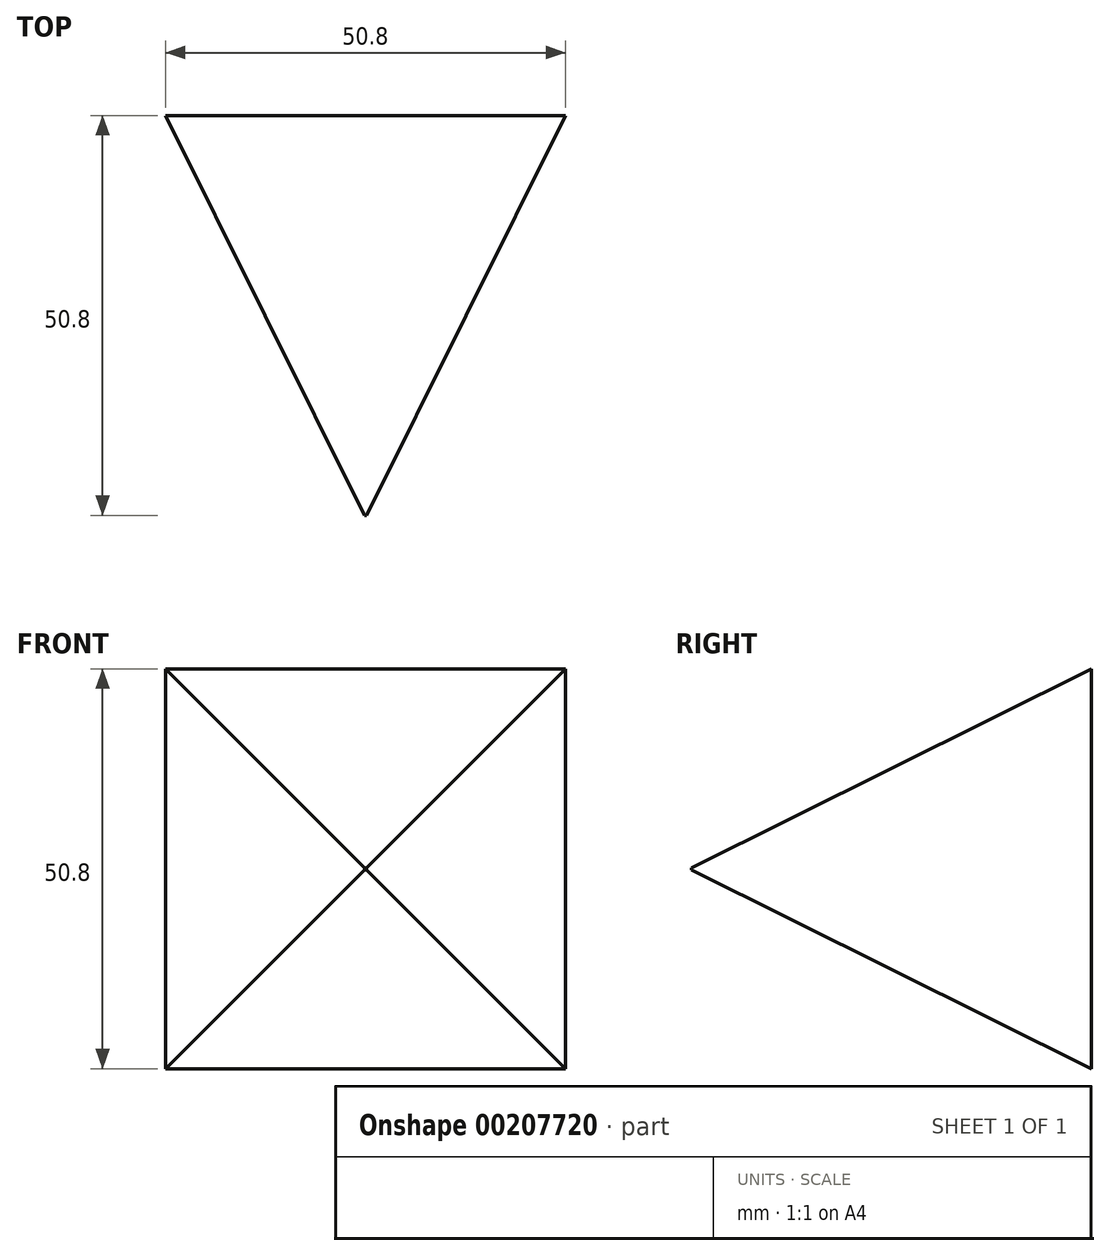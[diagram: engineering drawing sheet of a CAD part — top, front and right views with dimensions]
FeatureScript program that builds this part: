
annotation { "Feature Type Name" : "Feature", "Feature Type Description" : "" }
export const myFeature = defineFeature(function(context is Context, id is Id, definition is map)
    precondition{}
    {
        {
            var Q0;
            Q0=qCreatedBy(makeId("Front.planeOp"),FACE);
            var sketch = newSketch(context, id + "F0", { "sketchPlane" : qUnion([Q0])});
            skLineSegment(sketch, "E0.bottom", {"start": v(25.4, 25.4) * mm, "end": v(-25.4, 25.4) * mm});
            skLineSegment(sketch, "E0.top", {"start": v(25.4, -25.4) * mm, "end": v(-25.4, -25.4) * mm});
            skLineSegment(sketch, "E0.left", {"start": v(25.4, 25.4) * mm, "end": v(25.4, -25.4) * mm});
            skLineSegment(sketch, "E0.right", {"start": v(-25.4, 25.4) * mm, "end": v(-25.4, -25.4) * mm});
            skPoint(sketch, "E0.middle", {"position": v(0, 0) * mm});
            skSolve(sketch);
        }
        {
            var Q0;
            Q0=qCreatedBy(makeId("Front.planeOp"),FACE);
            cPlane(context, id + "F1", {"entities" : qUnion([Q0]), "cplaneType" : CPlaneType.OFFSET, "offset" : 50.8 * mm, "width" : 152.4 * mm, "height" : 152.4 * mm});
        }
        {
            var Q0;
            Q0=qCreatedBy(id+"F1.planeOp",FACE);
            var sketch = newSketch(context, id + "F2", { "sketchPlane" : qUnion([Q0])});
            skLineSegment(sketch, "E1.bottom", {"start": v(-0.13, 0.13) * mm, "end": v(0.13, 0.13) * mm});
            skLineSegment(sketch, "E1.top", {"start": v(-0.13, -0.13) * mm, "end": v(0.13, -0.13) * mm});
            skLineSegment(sketch, "E1.left", {"start": v(-0.13, 0.13) * mm, "end": v(-0.13, -0.13) * mm});
            skLineSegment(sketch, "E1.right", {"start": v(0.13, 0.13) * mm, "end": v(0.13, -0.13) * mm});
            skPoint(sketch, "E1.middle", {"position": v(0, 0) * mm});
            skSolve(sketch);
        }
        {
            var Q0;
            Q0 = qSketchRegion(id + "F2", true);
            var Q1;
            Q1 = qSketchRegion(id + "F0", true);
            loft(context, id + "F3", {"sheetProfilesArray" : [{ "sheetProfileEntities" : qUnion([Q0]) }, { "sheetProfileEntities" : qUnion([Q1]) }]});
        }
    });
